# Revit family: Bottle_Filler-Sensor_Operated-Murdock-BFI6_Series
name_source: partatom
category: Plumbing Fixtures
revit_build: Autodesk Revit 2018 (Build: 20170223_1515(x64)
units: mm (PartAtom-declared; Revit-internal decimal feet)

## family parameters
Cut with Voids When Loaded = Yes
Host = Face
OmniClass Number = 23.65.70.14.11
OmniClass Title = Drinking Fountains/Coolers
Part Type = Normal
Room Calculation Point = No
Round Connector Dimension = Use Diameter
Shared = Yes

## types (2) — shared parameters
110VAC Electrical Duplex Receptacle, by others = Yes
Assembly Code = D2010800
BAT - Battery Operated (N/A With Bottle Counter) = No
Basin Shape = Oval
Body Material = Metal-Murdock-304-Stainless_Steel
CW Connection = Yes
CWFU = 1.5
Cold Water Connection Diameter = 3/8"
Cold Water Connection Height = 26 1/4"
Cold Water Connection Radius = 3/16"
Cold Water Connection Width = 6 1/4"
Default Elevation = 34 1/2"
Description = Surface Mounted Sensor Operated Bottle Filler
Fill Rate = 1.1 GPM
Flow Rate = 1.00 GPM
HW Connection = Yes
Height = 29 1/2"
IAPMO Compliance = Certified to ANSI A117.1, Public Law 111-380 (NO-LEAD), CHSC
116875 and NSF/ANSI 61, Section 9.
Installation Type = Wall Mounted
LOGO - Customer Specified Logo / Graphics = No
Length = 18 1/4"
Manufacturer = Murdock Mfg.
Maximum Run Time = 20 Seconds
Pressure Range = 20 to 105 PSIG
Price = Prices may vary. Please consult Manufacturer Representative for most up-to-date price list.
Product Documentation Link = https://www.murdockmfg.com
Product Page URL = https://www.murdockmfg.com
Sink Material = Metal-Murdock-304-Stainless_Steel-Light_Grey
Transformer Specification = 120 VAC/9 VDC plug-in Transformer
URL = https://www.murdockmfg.com
Vent Connection = No
WF1 - 1500 gallon capacity, NSF 42+53, 1 micron Lead Reduction Water Filter = No
WF3 - 3000 gallon capacity, NSF 42+53, 1 micron Lead Reduction Water Filter = No
WFU = 2
Warranty Information = Murdock warrants that its products are free from defects in material or workmanship under normal use and service for a period of one year from date of shipment from the factory. Murdocks’s liability under this warranty shall be discharged solely by repair or replacement of defective material, provided Murdock is notified in writing within the time periods described above. This warranty does not cover installation or labor charges and does not apply to materials, which have been damaged by other causes such as mishandling or improper care or abnormal use. The repair or replacement of the defective materials shall constitute the sole remedy of the Buyer and the sole remedy of Murdock under this warranty. Murdock shall not be liable under any circumstances for incidental, consequential or direct charges caused by defects in the materials, or any delay in the repair or replacement thereof.  This warranty is in lieu of all other warranties expressed or implied. Product maintenance instructions are issued with each unit and disregard or non-compliance with these instructions will constitute an abnormal use condition and void the warranty. Stainless steel must be protected on jobsite during construction and must be properly maintained after the water has been introduced into the water cooler or drinking fountain, or Murdock’s limited warranty is void.
Waste Connection = Yes
Waste Connection Diameter = 1 1/2"
Waste Connection Height = 29 1/8"
Waste Connection Radius = 3/4"
Waste Connection Width = 3 1/2"
Width = 7 3/8"
zero-valued in all types: HWFU

## per-type parameters (varying)
| type | BCD - Bottle Counter Display |
| BF16 | No |
| BF16-BCD | Yes |

note: column(s) folded — value = type name in every type: Model

## geometry (parser evidence)
native form markers: Sweep x2
no freeform markers — native parametric forms only
